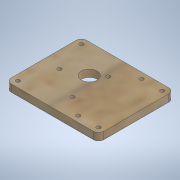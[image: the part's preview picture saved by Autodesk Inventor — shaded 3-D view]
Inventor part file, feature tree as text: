
AUTODESK INVENTOR PART (.ipt)
format: ipt  version: 2020.3 (Build 243373000, 373)  size: 171,520 bytes
history: native  units: mm
features: sketch x5, hole x3, extrude x2, other x1, fillet x1
ambient origin geometry x8: Origin, YZ Plane, XZ Plane, XY Plane, X Axis, Y Axis, Z Axis, Center Point
bodies: Body1 (feature_tree)
feature tree (12):
  other  "ソリッド1"
  extrude  "押し出し1"  Depth=5.5mm TaperAngle=0.0deg
  hole  "穴1"  [1 undecoded]
  fillet  "フィレット1"  Radius=57.0mm
  hole  "穴2"  [1 undecoded]
  extrude  "押し出し2"  Depth=4.5mm
  hole  "穴3"  [1 undecoded]
  sketch  "スケッチ1"
  sketch  "スケッチ2"
  sketch  "スケッチ3"
  sketch  "スケッチ4"
  sketch  "スケッチ5"
note: 3 required parameter values undecoded (feature->parameter linkage not recoverable at this tier; creation-order binding heuristic only, values carry confidence <= 0.55)
